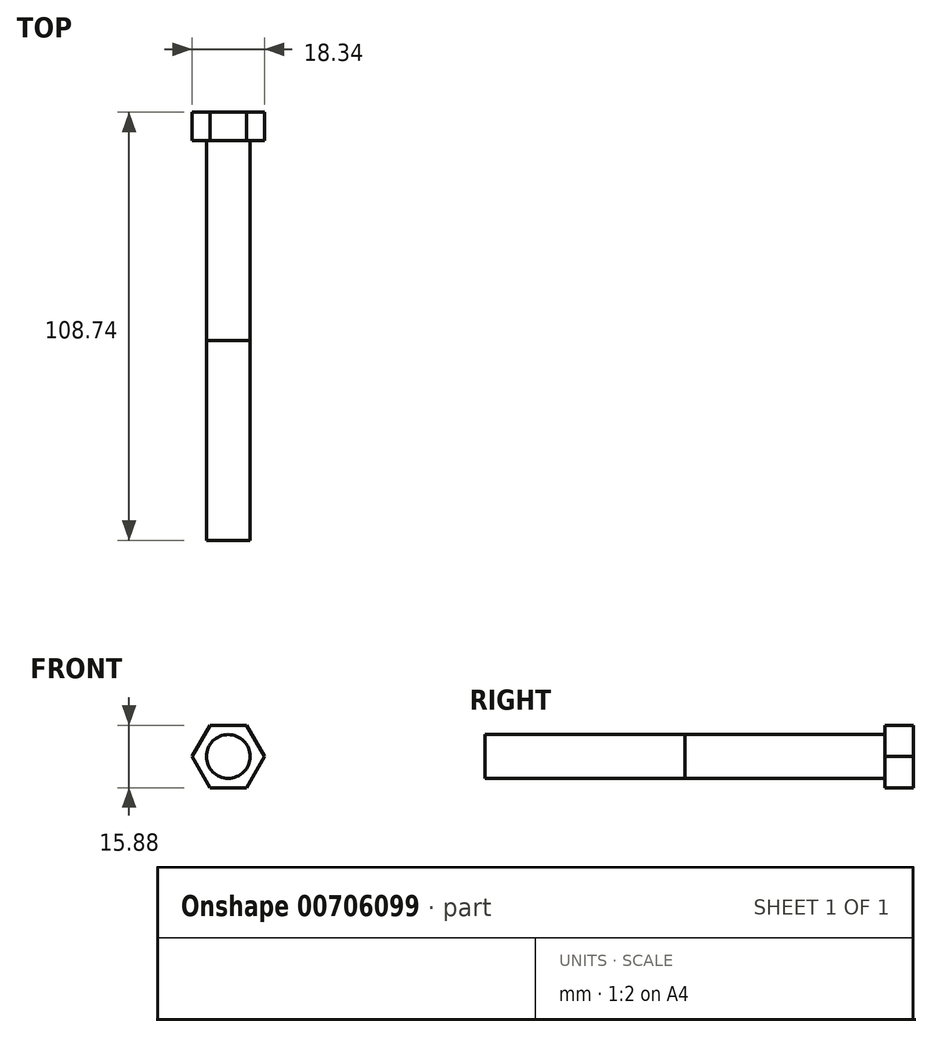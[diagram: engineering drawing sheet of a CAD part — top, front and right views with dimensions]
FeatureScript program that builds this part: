
annotation { "Feature Type Name" : "Feature", "Feature Type Description" : "" }
export const myFeature = defineFeature(function(context is Context, id is Id, definition is map)
    precondition{}
    {
        {
            var Q0;
            Q0=qCreatedBy(makeId("Front.planeOp"),FACE);
            var sketch = newSketch(context, id + "F0", { "sketchPlane" : qUnion([Q0])});
            skCircle(sketch, "E0.cCircle", {"center": v(0, 0) * mm, "radius": 7.94 * mm, "construction": true});
            skLineSegment(sketch, "E0.0", {"start": v(-4.58, 7.94) * mm, "end": v(4.58, 7.94) * mm});
            skLineSegment(sketch, "E0.1", {"start": v(4.58, 7.94) * mm, "end": v(9.17, 0) * mm});
            skLineSegment(sketch, "E0.2", {"start": v(9.17, 0) * mm, "end": v(4.58, -7.94) * mm});
            skLineSegment(sketch, "E0.3", {"start": v(4.58, -7.94) * mm, "end": v(-4.58, -7.94) * mm});
            skLineSegment(sketch, "E0.4", {"start": v(-4.58, -7.94) * mm, "end": v(-9.17, 0) * mm});
            skLineSegment(sketch, "E0.5", {"start": v(-9.17, 0) * mm, "end": v(-4.58, 7.94) * mm});
            skPoint(sketch, "E0.0.midPoint", {"position": v(0, 7.94) * mm});
            skSolve(sketch);
        }
        {
            var Q0;
            Q0 = qSketchRegion(id + "F0", true);
            extrude(context, id + "F1", {"entities" : qUnion([Q0]), "depth" : 7.14 * mm, "offsetDistance" : 25.4 * mm});
        }
        {
            var Q0;
            Q0=makeQuery(id+"F1.opExtrude","CAP_FACE",FACE,{"disambiguationData":[OSD([sQuery(id+"F0.wireOp",EDGE,"E0.0"),sQuery(id+"F0.wireOp",EDGE,"E0.1"),sQuery(id+"F0.wireOp",EDGE,"E0.2"),sQuery(id+"F0.wireOp",EDGE,"E0.3"),sQuery(id+"F0.wireOp",EDGE,"E0.4"),sQuery(id+"F0.wireOp",EDGE,"E0.5")])],"isStart":false});
            var sketch = newSketch(context, id + "F2", { "sketchPlane" : qUnion([Q0])});
            skCircle(sketch, "E1", {"center": v(0, 0) * mm, "radius": 5.56 * mm});
            skSolve(sketch);
        }
        {
            var Q0;
            Q0 = qSketchRegion(id + "F2", true);
            extrude(context, id + "F3", {"entities" : qUnion([Q0]), "operationType" : NewBodyOperationType.ADD, "depth" : 50.8 * mm, "offsetDistance" : 25.4 * mm});
        }
        {
            var Q0;
            Q0=makeQuery(id+"F3.opExtrude","CAP_FACE",FACE,{"disambiguationData":[OSD([sQuery(id+"F2.wireOp",EDGE,"E1")])],"isStart":false});
            var sketch = newSketch(context, id + "F4", { "sketchPlane" : qUnion([Q0])});
            skCircle(sketch, "E2", {"center": v(0, 0) * mm, "radius": 5.56 * mm});
            skSolve(sketch);
        }
        {
            var Q0;
            Q0 = qSketchRegion(id + "F4", true);
            extrude(context, id + "F5", {"entities" : qUnion([Q0]), "depth" : 50.8 * mm, "offsetDistance" : 25.4 * mm, "hasSecondDirection" : true, "secondDirectionOppositeDirection" : false, "secondDirectionDepth" : 0 * mm});
        }
    });
